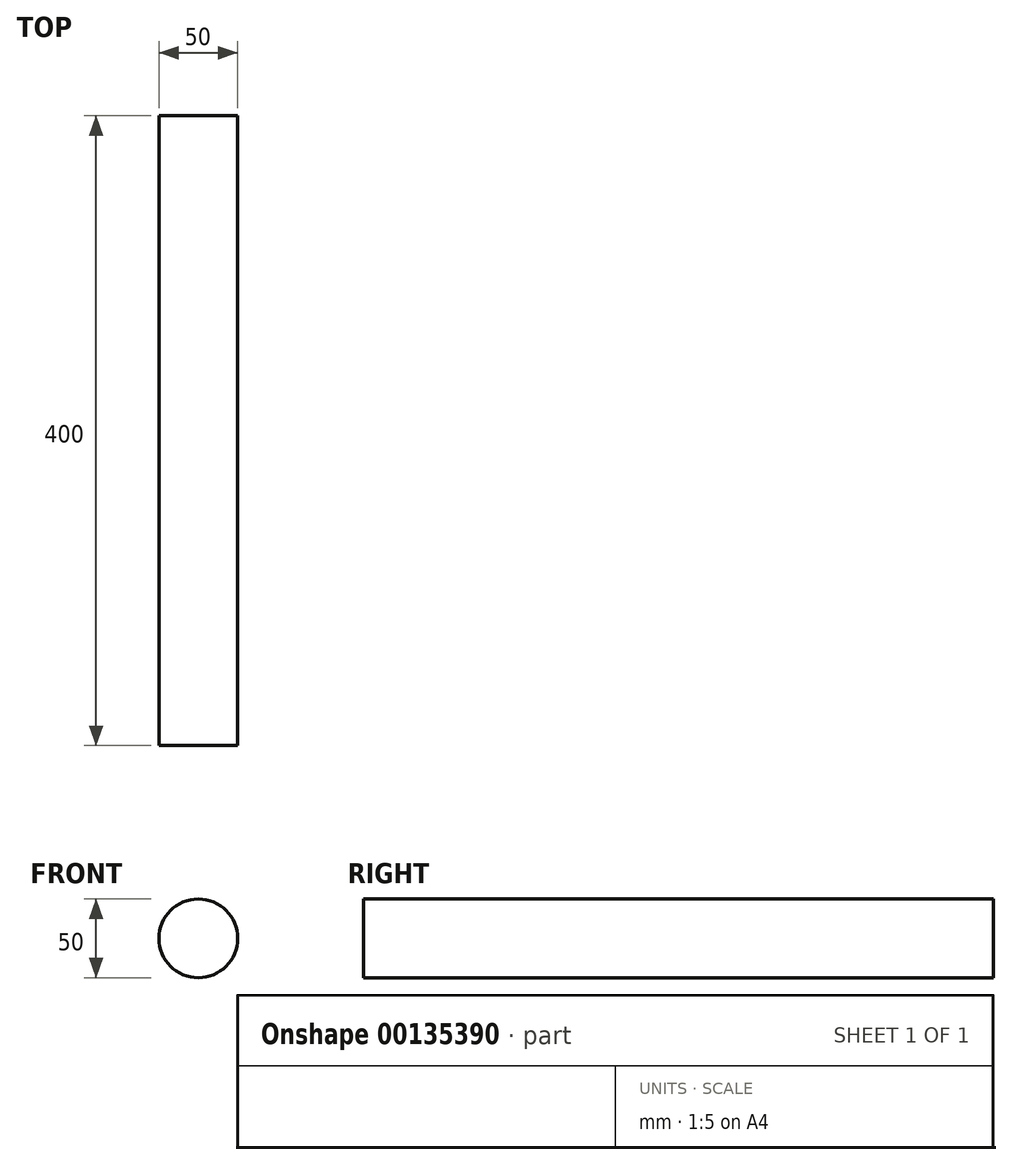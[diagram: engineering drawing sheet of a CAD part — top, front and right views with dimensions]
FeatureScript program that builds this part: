
annotation { "Feature Type Name" : "Feature", "Feature Type Description" : "" }
export const myFeature = defineFeature(function(context is Context, id is Id, definition is map)
    precondition{}
    {
        {
            var Q0;
            Q0=qCreatedBy(makeId("Front.planeOp"),FACE);
            var sketch = newSketch(context, id + "F0", { "sketchPlane" : qUnion([Q0])});
            skCircle(sketch, "E0", {"center": v(0, 0) * mm, "radius": 25 * mm});
            skSolve(sketch);
        }
        {
            var Q0;
            Q0=qSketchRegion(id+"F0",true);
            extrude(context, id + "F1", {"entities" : qUnion([Q0]), "depth" : 400 * mm});
        }
    });
